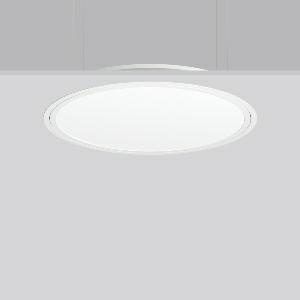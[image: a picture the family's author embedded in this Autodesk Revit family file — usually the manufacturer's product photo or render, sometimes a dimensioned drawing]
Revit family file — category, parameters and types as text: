
# Revit family: triona_round_e_312383_002_2_12_485d
name_source: partatom
category: Lighting Fixtures
units: mm (PartAtom-declared; Revit-internal decimal feet)

## family parameters
Cut with Voids When Loaded = No
Host = Face
Light Source = No
Part Type = Normal
Room Calculation Point = No
Round Connector Dimension = Use Diameter
Shared = No

## types (1)
- TuneableWhite 846 (1 x LED Modul 846, 3350 lm, 4600)
    Apparent Load = 40 VA
    CIE Flux Codes = 50 80 96 100 100
    Color Rendering = 80
    Color Temperature = 4600
    Default Elevation = 1800 mm
    Description = Series: TRIONA round
Decorative round LED recessed surface luminaire. Cover made of sheet steel, powder-coated. Frame made of aluminium, powder-coated. Recessed ring: aluminium extrusion profile, powder coated. Light emission through a diffuser: plastic, opal. Lightguide and diffuser made of non-yellowing plastic (PMMA). Lateral light emission (RZB SIDELITE technology) for above-average homogeneous light distribution. Tunable white versions, dynamically adjustable from 2700 K to 6500 K. Suitable for installation in cavity ceilings. Tool-free mounting system thanks to the rocker arm mechanism (patent pending). Electronic ballast included. Very easy installation thanks to Plug+Play connection. Ideal for use as part of the Human Centric Lighting concept in connection with RZB light management systems. 
Colour: traffic white, matt (RAL 9016)
Diameter: 725 mm
Height: 2 mm
Cut-out diameter: 702 mm
Recess height: 100 mm
Luminaire: recess height: 89 mm
Lamp: LED
Socket: without socket
Colour temperature: 2700K - 6500K
Colour rendering index (CRI): 80
System power: 40 W
Rated luminous flux: 3350 lm
Luminous efficiency: 84 lm/W
System power 2: 42 W
Rated luminous flux 2: 3200 lm
Luminous efficiency 2: 76 lm/W
System power 3: 42 W
Rated luminous flux 3: 3250 lm
Luminous efficiency 3: 77 lm/W
Control gear: Converter, dimmable, DALI
Protection class: I
Type of protection: IP 40
    Height = 0 mm  [stored 0 ft]
    Lamp = 1 x LED Modul 846
    Lamp Light Flux = 3350 lm
    Lamp count = 1
    Length = 725 mm
    Lifetime = 50000 h
    Luminous efficacy = 84 lm/W
    Manufacturer = RZB
    ModVariant = No
    Model = 312383.002.2.12
    Mounting Place = Ceiling
    Mounting Type = Recessed
    Number of Poles = 1
    OnlyDefault = Yes
    Power Factor = 1
    Product Name = TRIONA round E
    Product group = Recessed modular luminaires
    ProductGroupID = 406
    Protection Class = Protection class I
    Protection Degree = IP 20
    RLX_Detail_Level = 1
    RLX_Emergency_Light_Flux = 0 lm
    RLX_Emergency_Type = 0
    RLX_Emergency_Type_DB = No
    RlxData = <blob elided: 35273 chars, md5=1b9b2679>
    Socket = socket
    Standby Power = 0 W
    System Light Flux = 3350 lm
    System Power = 40 W
    Type Comments = TuneableWhite 846
    Type Image = 312383.002.12.jpg
    URL = http://relux.com
    VarID = tuneablewhite_846
    Voltage = 230 V
    Voltage Range = 220-240 V
    Weight = 0.00 kg
    Width = 0 mm  [stored 0 ft]

note: [stored X ft] marks values corroborated as IEEE doubles in the binary element streams (Revit-internal decimal feet)

## geometry (parser evidence)
native form markers: Blend x4, Sweep x8
no freeform markers — native parametric forms only
